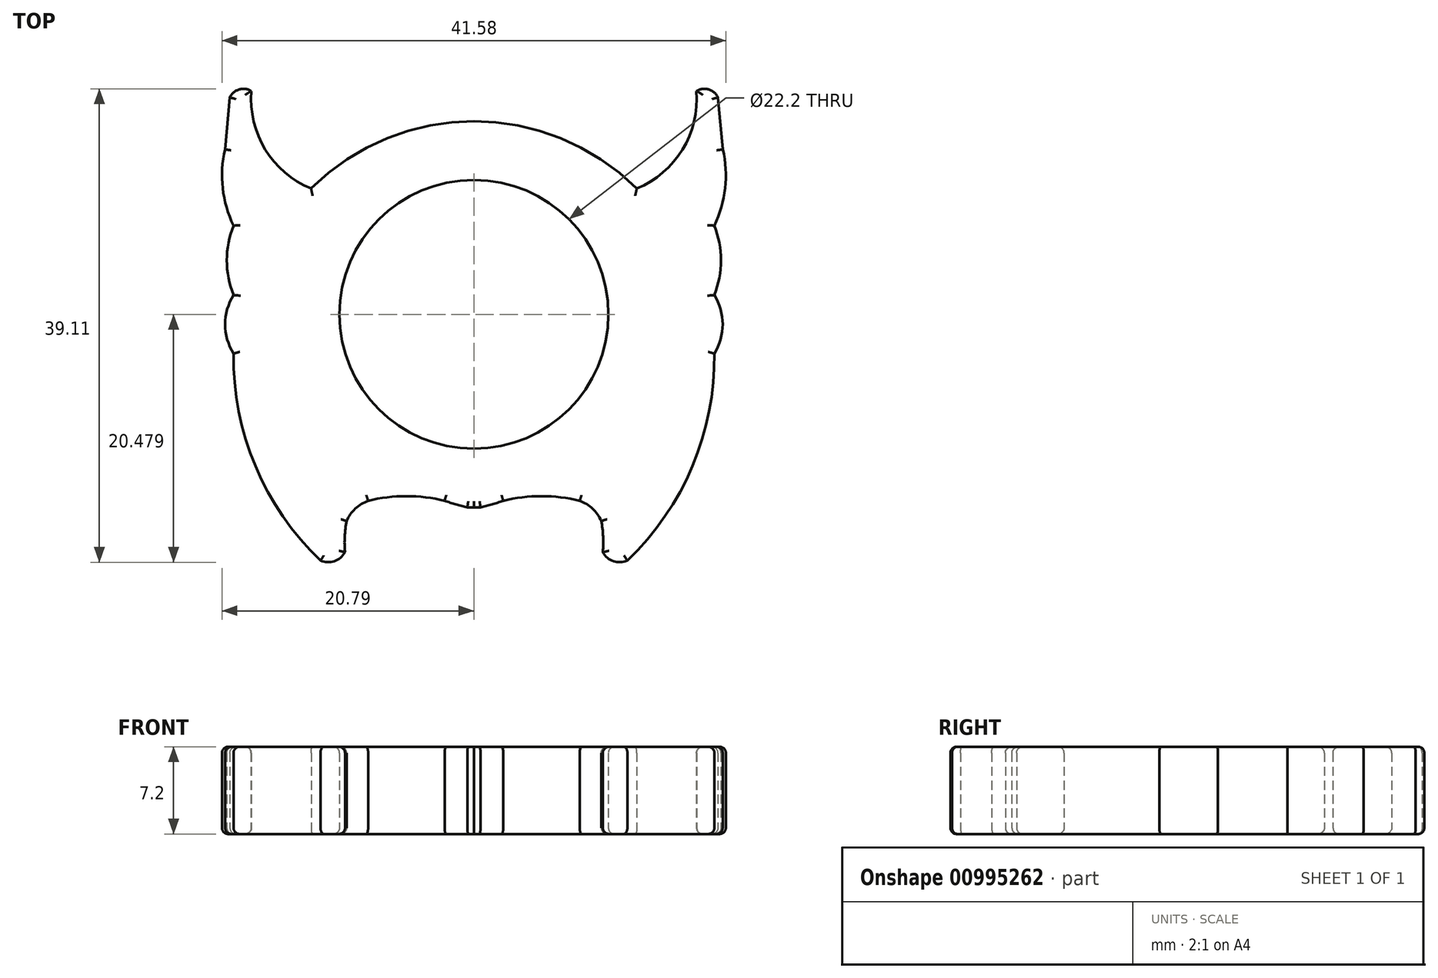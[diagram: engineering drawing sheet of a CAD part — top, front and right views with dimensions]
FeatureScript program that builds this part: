
annotation { "Feature Type Name" : "Feature", "Feature Type Description" : "" }
export const myFeature = defineFeature(function(context is Context, id is Id, definition is map)
    precondition{}
    {
        {
            var Q0;
            Q0=qCreatedBy(makeId("Top.planeOp"),FACE);
            var sketch = newSketch(context, id + "F0", { "sketchPlane" : qUnion([Q0])});
            skPoint(sketch, "E0.third.point", {"position": v(0, 14.77) * mm});
            skArc(sketch, "E1", {"start": v(0, 15.44) * mm, "mid": v(-7.27, 14) * mm, "end": v(-13.44, 9.89) * mm});
            skPoint(sketch, "E1.first.point", {"position": v(-13.44, 9.89) * mm});
            skPoint(sketch, "E1.second.point", {"position": v(13.44, 9.89) * mm});
            skPoint(sketch, "E1.third.point", {"position": v(12.46, -18.01) * mm});
            skPoint(sketch, "E2.second.point", {"position": v(-18.32, 17.94) * mm});
            skPoint(sketch, "E2.third.point", {"position": v(-7.15, 24.14) * mm});
            skArc(sketch, "E3", {"start": v(13.44, 9.89) * mm, "mid": v(17.22, 13.11) * mm, "end": v(18.37, 17.94) * mm});
            skPoint(sketch, "E3.second.point", {"position": v(18.37, 17.94) * mm});
            skPoint(sketch, "E3.third.point", {"position": v(6.28, 24.14) * mm});
            skArc(sketch, "E4", {"start": v(20.14, 17.42) * mm, "mid": v(19.37, 18.08) * mm, "end": v(18.37, 17.94) * mm});
            skLineSegment(sketch, "E5", {"start": v(20.14, 17.42) * mm, "end": v(20.54, 13.13) * mm});
            skArc(sketch, "E6", {"start": v(19.84, 6.83) * mm, "mid": v(20.74, 9.92) * mm, "end": v(20.54, 13.13) * mm});
            skArc(sketch, "E7", {"start": v(19.84, 1.1) * mm, "mid": v(20.4, 3.96) * mm, "end": v(19.84, 6.83) * mm});
            skArc(sketch, "E8", {"start": v(19.84, -3.74) * mm, "mid": v(20.53, -1.33) * mm, "end": v(19.84, 1.1) * mm});
            skArc(sketch, "E9", {"start": v(12.67, -20.85) * mm, "mid": v(18.04, -13.04) * mm, "end": v(19.84, -3.74) * mm});
            skArc(sketch, "E10", {"start": v(10.64, -20.15) * mm, "mid": v(11.52, -20.9) * mm, "end": v(12.67, -20.85) * mm});
            skArc(sketch, "E11", {"start": v(10.64, -20.15) * mm, "mid": v(10.67, -18.86) * mm, "end": v(10.51, -17.58) * mm});
            skArc(sketch, "E12", {"start": v(10.51, -17.58) * mm, "mid": v(9.8, -16.56) * mm, "end": v(8.73, -15.91) * mm});
            skArc(sketch, "E13", {"start": v(8.73, -15.91) * mm, "mid": v(5.58, -15.52) * mm, "end": v(2.42, -15.91) * mm});
            skArc(sketch, "E14", {"start": v(0.54, -16.44) * mm, "mid": v(1.49, -16.2) * mm, "end": v(2.42, -15.91) * mm});
            skArc(sketch, "E15", {"start": v(0, -16.44) * mm, "mid": v(0.27, -16.45) * mm, "end": v(0.54, -16.44) * mm});
            skLineSegment(sketch, "E16", {"start": v(0, 0) * mm, "end": v(0, 14.77) * mm, "construction": true});
            skArc(sketch, "E17.MirrorCS", {"start": v(0, 15.44) * mm, "mid": v(7.27, 14) * mm, "end": v(13.44, 9.89) * mm});
            skArc(sketch, "E18.MirrorCS", {"start": v(-13.44, 9.89) * mm, "mid": v(-17.22, 13.11) * mm, "end": v(-18.37, 17.94) * mm});
            skArc(sketch, "E19.MirrorCS", {"start": v(-20.14, 17.42) * mm, "mid": v(-19.37, 18.08) * mm, "end": v(-18.37, 17.94) * mm});
            skLineSegment(sketch, "E20.MirrorCS", {"start": v(-20.14, 17.42) * mm, "end": v(-20.54, 13.13) * mm});
            skArc(sketch, "E21.MirrorCS", {"start": v(-19.84, 6.83) * mm, "mid": v(-20.74, 9.92) * mm, "end": v(-20.54, 13.13) * mm});
            skArc(sketch, "E22.MirrorCS", {"start": v(-19.84, 1.1) * mm, "mid": v(-20.4, 3.96) * mm, "end": v(-19.84, 6.83) * mm});
            skArc(sketch, "E23.MirrorCS", {"start": v(-19.84, -3.74) * mm, "mid": v(-20.53, -1.33) * mm, "end": v(-19.84, 1.1) * mm});
            skArc(sketch, "E24.MirrorCS", {"start": v(-12.67, -20.85) * mm, "mid": v(-18.04, -13.04) * mm, "end": v(-19.84, -3.74) * mm});
            skArc(sketch, "E25.MirrorCS", {"start": v(-10.64, -20.15) * mm, "mid": v(-10.67, -18.86) * mm, "end": v(-10.51, -17.58) * mm});
            skArc(sketch, "E26.MirrorCS", {"start": v(-10.64, -20.15) * mm, "mid": v(-11.52, -20.9) * mm, "end": v(-12.67, -20.85) * mm});
            skArc(sketch, "E27.MirrorCS", {"start": v(-10.51, -17.58) * mm, "mid": v(-9.8, -16.56) * mm, "end": v(-8.73, -15.91) * mm});
            skArc(sketch, "E28.MirrorCS", {"start": v(-8.73, -15.91) * mm, "mid": v(-5.58, -15.52) * mm, "end": v(-2.42, -15.91) * mm});
            skArc(sketch, "E29.MirrorCS", {"start": v(-0.54, -16.44) * mm, "mid": v(-1.49, -16.2) * mm, "end": v(-2.42, -15.91) * mm});
            skArc(sketch, "E30.MirrorCS", {"start": v(0, -16.44) * mm, "mid": v(-0.27, -16.45) * mm, "end": v(-0.54, -16.44) * mm});
            skLineSegment(sketch, "E31", {"start": v(0, 15.44) * mm, "end": v(0, -16.44) * mm, "construction": true});
            skLineSegment(sketch, "E32", {"start": v(0, -0.5) * mm, "end": v(-1.05, -0.5) * mm, "construction": true});
            skCircle(sketch, "E33", {"center": v(0, -0.5) * mm, "radius": 11.1 * mm});
            skSolve(sketch);
        }
        {
            var Q0;
            Q0 = qSketchRegion(id + "F0", true);
            extrude(context, id + "F1", {"entities" : qUnion([Q0]), "depth" : 7.2 * mm, "offsetDistance" : 25 * mm});
        }
        {
            var Q0;
            Q0=makeQuery(id+"F1.opExtrude","CAP_FACE",FACE,{"disambiguationData":[OSD([sQuery(id+"F0.wireOp",EDGE,"E1"),sQuery(id+"F0.wireOp",EDGE,"E3"),sQuery(id+"F0.wireOp",EDGE,"E4"),sQuery(id+"F0.wireOp",EDGE,"E5"),sQuery(id+"F0.wireOp",EDGE,"E6"),sQuery(id+"F0.wireOp",EDGE,"E7"),sQuery(id+"F0.wireOp",EDGE,"E8"),sQuery(id+"F0.wireOp",EDGE,"E9"),sQuery(id+"F0.wireOp",EDGE,"E10"),sQuery(id+"F0.wireOp",EDGE,"E11"),sQuery(id+"F0.wireOp",EDGE,"E12"),sQuery(id+"F0.wireOp",EDGE,"E13"),sQuery(id+"F0.wireOp",EDGE,"E14"),sQuery(id+"F0.wireOp",EDGE,"E15"),sQuery(id+"F0.wireOp",EDGE,"E17.MirrorCS"),sQuery(id+"F0.wireOp",EDGE,"E18.MirrorCS"),sQuery(id+"F0.wireOp",EDGE,"E20.MirrorCS"),sQuery(id+"F0.wireOp",EDGE,"E19.MirrorCS"),sQuery(id+"F0.wireOp",EDGE,"E21.MirrorCS"),sQuery(id+"F0.wireOp",EDGE,"E22.MirrorCS"),sQuery(id+"F0.wireOp",EDGE,"E23.MirrorCS"),sQuery(id+"F0.wireOp",EDGE,"E24.MirrorCS"),sQuery(id+"F0.wireOp",EDGE,"E25.MirrorCS"),sQuery(id+"F0.wireOp",EDGE,"E26.MirrorCS"),sQuery(id+"F0.wireOp",EDGE,"E27.MirrorCS"),sQuery(id+"F0.wireOp",EDGE,"E28.MirrorCS"),sQuery(id+"F0.wireOp",EDGE,"E29.MirrorCS"),sQuery(id+"F0.wireOp",EDGE,"E30.MirrorCS"),sQuery(id+"F0.wireOp",EDGE,"E33")])],"isStart":false});
            var Q1;
            Q1=makeQuery(id+"F1.opExtrude","CAP_FACE",FACE,{"disambiguationData":[OSD([sQuery(id+"F0.wireOp",EDGE,"E1"),sQuery(id+"F0.wireOp",EDGE,"E3"),sQuery(id+"F0.wireOp",EDGE,"E4"),sQuery(id+"F0.wireOp",EDGE,"E5"),sQuery(id+"F0.wireOp",EDGE,"E6"),sQuery(id+"F0.wireOp",EDGE,"E7"),sQuery(id+"F0.wireOp",EDGE,"E8"),sQuery(id+"F0.wireOp",EDGE,"E9"),sQuery(id+"F0.wireOp",EDGE,"E10"),sQuery(id+"F0.wireOp",EDGE,"E11"),sQuery(id+"F0.wireOp",EDGE,"E12"),sQuery(id+"F0.wireOp",EDGE,"E13"),sQuery(id+"F0.wireOp",EDGE,"E14"),sQuery(id+"F0.wireOp",EDGE,"E15"),sQuery(id+"F0.wireOp",EDGE,"E17.MirrorCS"),sQuery(id+"F0.wireOp",EDGE,"E18.MirrorCS"),sQuery(id+"F0.wireOp",EDGE,"E20.MirrorCS"),sQuery(id+"F0.wireOp",EDGE,"E19.MirrorCS"),sQuery(id+"F0.wireOp",EDGE,"E21.MirrorCS"),sQuery(id+"F0.wireOp",EDGE,"E22.MirrorCS"),sQuery(id+"F0.wireOp",EDGE,"E23.MirrorCS"),sQuery(id+"F0.wireOp",EDGE,"E24.MirrorCS"),sQuery(id+"F0.wireOp",EDGE,"E25.MirrorCS"),sQuery(id+"F0.wireOp",EDGE,"E26.MirrorCS"),sQuery(id+"F0.wireOp",EDGE,"E27.MirrorCS"),sQuery(id+"F0.wireOp",EDGE,"E28.MirrorCS"),sQuery(id+"F0.wireOp",EDGE,"E29.MirrorCS"),sQuery(id+"F0.wireOp",EDGE,"E30.MirrorCS"),sQuery(id+"F0.wireOp",EDGE,"E33")])],"isStart":true});
            fillet(context, id + "F2", {"entities" : qUnion([Q0, Q1]), "radius" : 0.5 * mm, "tangentPropagation" : true, "allowEdgeOverflow" : false});
        }
    });
